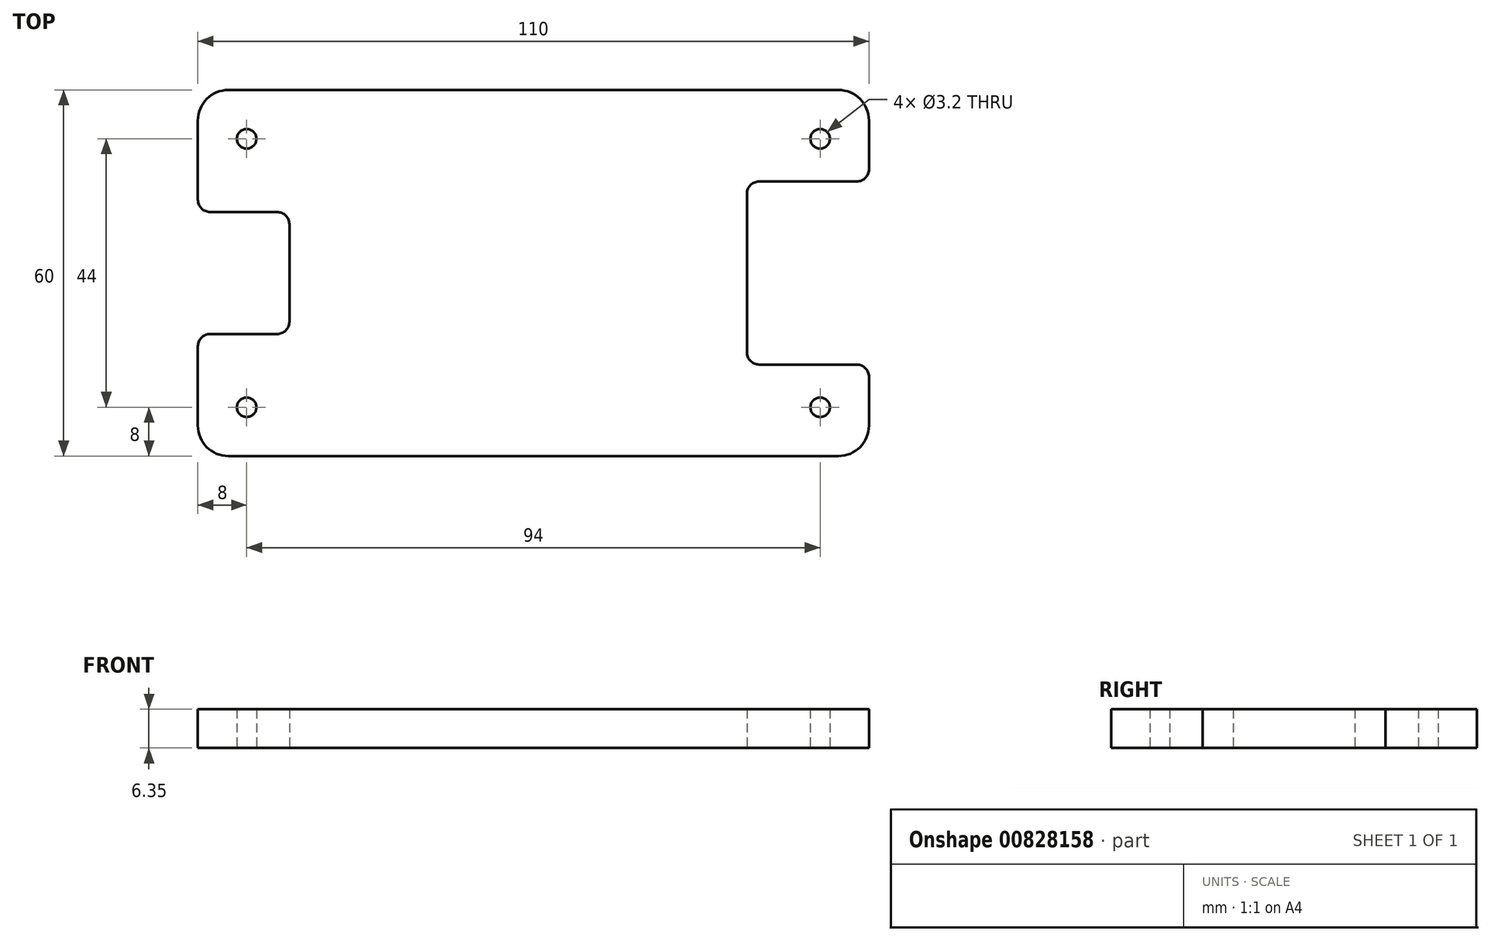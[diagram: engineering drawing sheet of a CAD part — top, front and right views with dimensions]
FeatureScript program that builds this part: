
annotation { "Feature Type Name" : "Feature", "Feature Type Description" : "" }
export const myFeature = defineFeature(function(context is Context, id is Id, definition is map)
    precondition{}
    {
        {
            var Q0;
            Q0=qCreatedBy(makeId("Top.planeOp"),FACE);
            var sketch = newSketch(context, id + "F0", { "sketchPlane" : qUnion([Q0])});
            skLineSegment(sketch, "E0.bottom", {"start": v(-55, 30) * mm, "end": v(55, 30) * mm});
            skLineSegment(sketch, "E0.top", {"start": v(-55, -30) * mm, "end": v(55, -30) * mm});
            skLineSegment(sketch, "E0.left", {"start": v(-55, 30) * mm, "end": v(-55, 10) * mm});
            skLineSegment(sketch, "E0.right", {"start": v(55, 30) * mm, "end": v(55, 15) * mm});
            skCircle(sketch, "E1", {"center": v(-47, 22) * mm, "radius": 1.6 * mm});
            skCircle(sketch, "E2", {"center": v(47, 22) * mm, "radius": 1.6 * mm});
            skCircle(sketch, "E3", {"center": v(-47, -22) * mm, "radius": 1.6 * mm});
            skCircle(sketch, "E4", {"center": v(47, -22) * mm, "radius": 1.6 * mm});
            skLineSegment(sketch, "E5", {"start": v(-55, 10) * mm, "end": v(-40, 10) * mm});
            skLineSegment(sketch, "E6", {"start": v(-40, 10) * mm, "end": v(-40, -10) * mm});
            skLineSegment(sketch, "E7", {"start": v(-40, -10) * mm, "end": v(-55, -10) * mm});
            skLineSegment(sketch, "E8.trimOffspring", {"start": v(-55, -10) * mm, "end": v(-55, -30) * mm});
            skLineSegment(sketch, "E9", {"start": v(55, 15) * mm, "end": v(35, 15) * mm});
            skLineSegment(sketch, "E10", {"start": v(35, 15) * mm, "end": v(35, -15) * mm});
            skLineSegment(sketch, "E11", {"start": v(35, -15) * mm, "end": v(55, -15) * mm});
            skLineSegment(sketch, "E12.trimOffspring", {"start": v(55, -15) * mm, "end": v(55, -30) * mm});
            skSolve(sketch);
        }
        {
            var Q0;
            Q0=makeQuery(id+"F0.imprint","IMPRINT",FACE,{"disambiguationData":[TD([[makeQuery(id+"F0.imprint","IMPRINT",EDGE,{"derivedFrom":sQuery(id+"F0.wireOp",EDGE,"E0.bottom")}),-1.0]])]});
            extrude(context, id + "F1", {"entities" : qUnion([Q0]), "depth" : 6.35 * mm, "offsetDistance" : 25 * mm});
        }
        {
            var Q0;
            Q0=makeQuery(id+"F1.opExtrude","SWEPT_EDGE",EDGE,{"disambiguationData":[OSD([sQuery(id+"F0.wireOp",EDGE,"E0.bottom"),sQuery(id+"F0.wireOp",EDGE,"E0.left")])]});
            var Q1;
            Q1=makeQuery(id+"F1.opExtrude","SWEPT_EDGE",EDGE,{"disambiguationData":[OSD([sQuery(id+"F0.wireOp",EDGE,"E0.bottom"),sQuery(id+"F0.wireOp",EDGE,"E0.right")])]});
            var Q2;
            Q2=makeQuery(id+"F1.opExtrude","SWEPT_EDGE",EDGE,{"disambiguationData":[OSD([sQuery(id+"F0.wireOp",EDGE,"E0.top"),sQuery(id+"F0.wireOp",EDGE,"E12.trimOffspring")])]});
            var Q3;
            Q3=makeQuery(id+"F1.opExtrude","SWEPT_EDGE",EDGE,{"disambiguationData":[OSD([sQuery(id+"F0.wireOp",EDGE,"E0.top"),sQuery(id+"F0.wireOp",EDGE,"E8.trimOffspring")])]});
            fillet(context, id + "F2", {"entities" : qUnion([Q0, Q1, Q2, Q3]), "radius" : 5 * mm, "tangentPropagation" : true, "allowEdgeOverflow" : false});
        }
        {
            var Q0;
            Q0=makeQuery(id+"F1.opExtrude","SWEPT_EDGE",EDGE,{"disambiguationData":[OSD([sQuery(id+"F0.wireOp",EDGE,"E7"),sQuery(id+"F0.wireOp",EDGE,"E8.trimOffspring")])]});
            var Q1;
            Q1=makeQuery(id+"F1.opExtrude","SWEPT_EDGE",EDGE,{"disambiguationData":[OSD([sQuery(id+"F0.wireOp",EDGE,"E6"),sQuery(id+"F0.wireOp",EDGE,"E7")])]});
            var Q2;
            Q2=makeQuery(id+"F1.opExtrude","SWEPT_EDGE",EDGE,{"disambiguationData":[OSD([sQuery(id+"F0.wireOp",EDGE,"E0.left"),sQuery(id+"F0.wireOp",EDGE,"E5")])]});
            var Q3;
            Q3=makeQuery(id+"F1.opExtrude","SWEPT_EDGE",EDGE,{"disambiguationData":[OSD([sQuery(id+"F0.wireOp",EDGE,"E5"),sQuery(id+"F0.wireOp",EDGE,"E6")])]});
            var Q4;
            Q4=makeQuery(id+"F1.opExtrude","SWEPT_EDGE",EDGE,{"disambiguationData":[OSD([sQuery(id+"F0.wireOp",EDGE,"E10"),sQuery(id+"F0.wireOp",EDGE,"E11")])]});
            var Q5;
            Q5=makeQuery(id+"F1.opExtrude","SWEPT_EDGE",EDGE,{"disambiguationData":[OSD([sQuery(id+"F0.wireOp",EDGE,"E11"),sQuery(id+"F0.wireOp",EDGE,"E12.trimOffspring")])]});
            var Q6;
            Q6=makeQuery(id+"F1.opExtrude","SWEPT_EDGE",EDGE,{"disambiguationData":[OSD([sQuery(id+"F0.wireOp",EDGE,"E0.right"),sQuery(id+"F0.wireOp",EDGE,"E9")])]});
            var Q7;
            Q7=makeQuery(id+"F1.opExtrude","SWEPT_EDGE",EDGE,{"disambiguationData":[OSD([sQuery(id+"F0.wireOp",EDGE,"E9"),sQuery(id+"F0.wireOp",EDGE,"E10")])]});
            fillet(context, id + "F3", {"entities" : qUnion([Q0, Q1, Q2, Q3, Q4, Q5, Q6, Q7]), "radius" : 2 * mm, "tangentPropagation" : true, "allowEdgeOverflow" : false});
        }
    });
